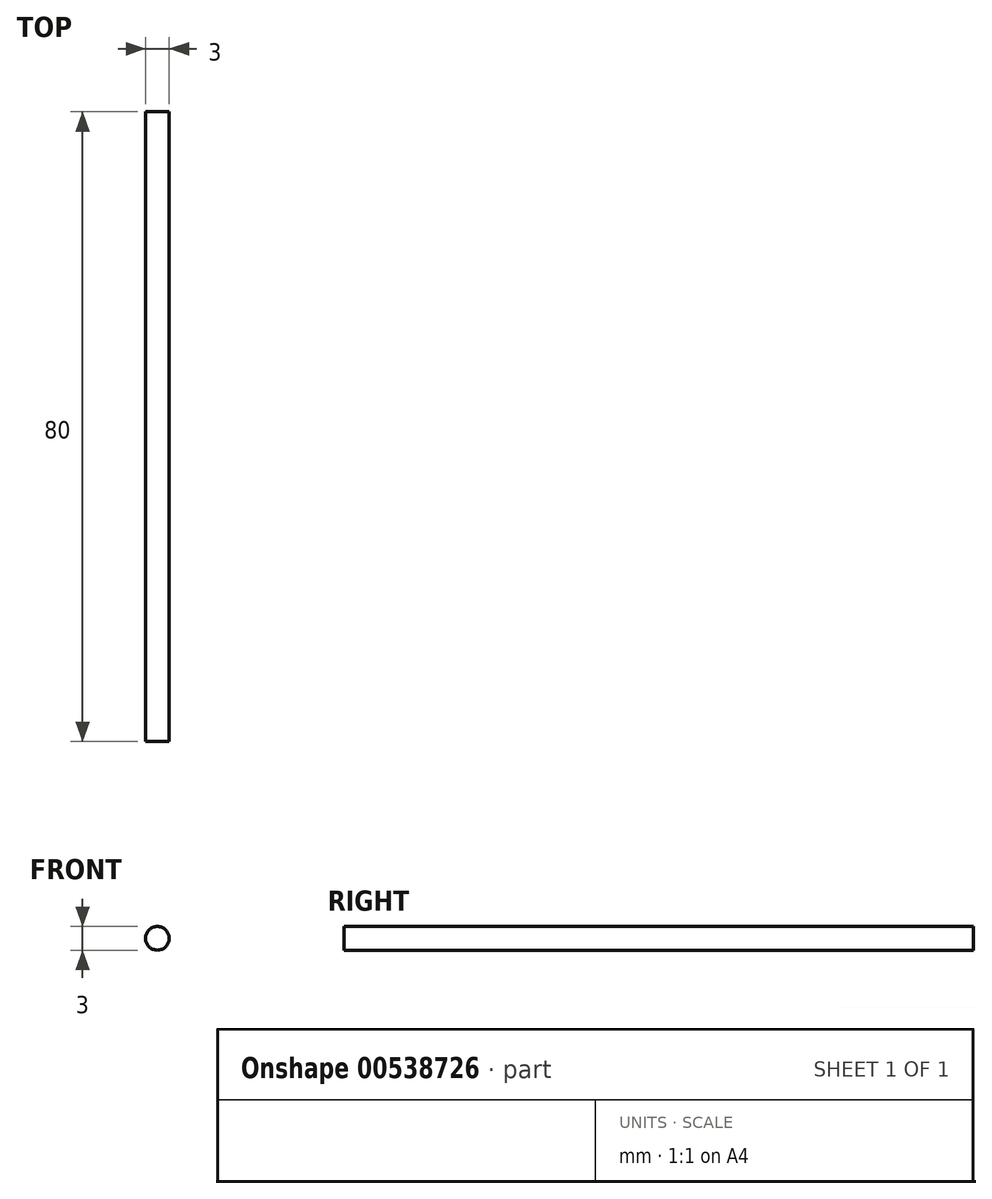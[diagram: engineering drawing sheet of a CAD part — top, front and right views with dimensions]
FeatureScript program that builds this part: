
annotation { "Feature Type Name" : "Feature", "Feature Type Description" : "" }
export const myFeature = defineFeature(function(context is Context, id is Id, definition is map)
    precondition{}
    {
        {
            var Q0;
            Q0=qCreatedBy(makeId("Front.planeOp"),FACE);
            var sketch = newSketch(context, id + "F0", { "sketchPlane" : qUnion([Q0])});
            skCircle(sketch, "E0", {"center": v(0, 0) * mm, "radius": 1.5 * mm});
            skSolve(sketch);
        }
        {
            var Q0;
            Q0 = qSketchRegion(id + "F0", true);
            extrude(context, id + "F1", {"entities" : qUnion([Q0]), "depth" : 80 * mm, "offsetDistance" : 25 * mm});
        }
    });
